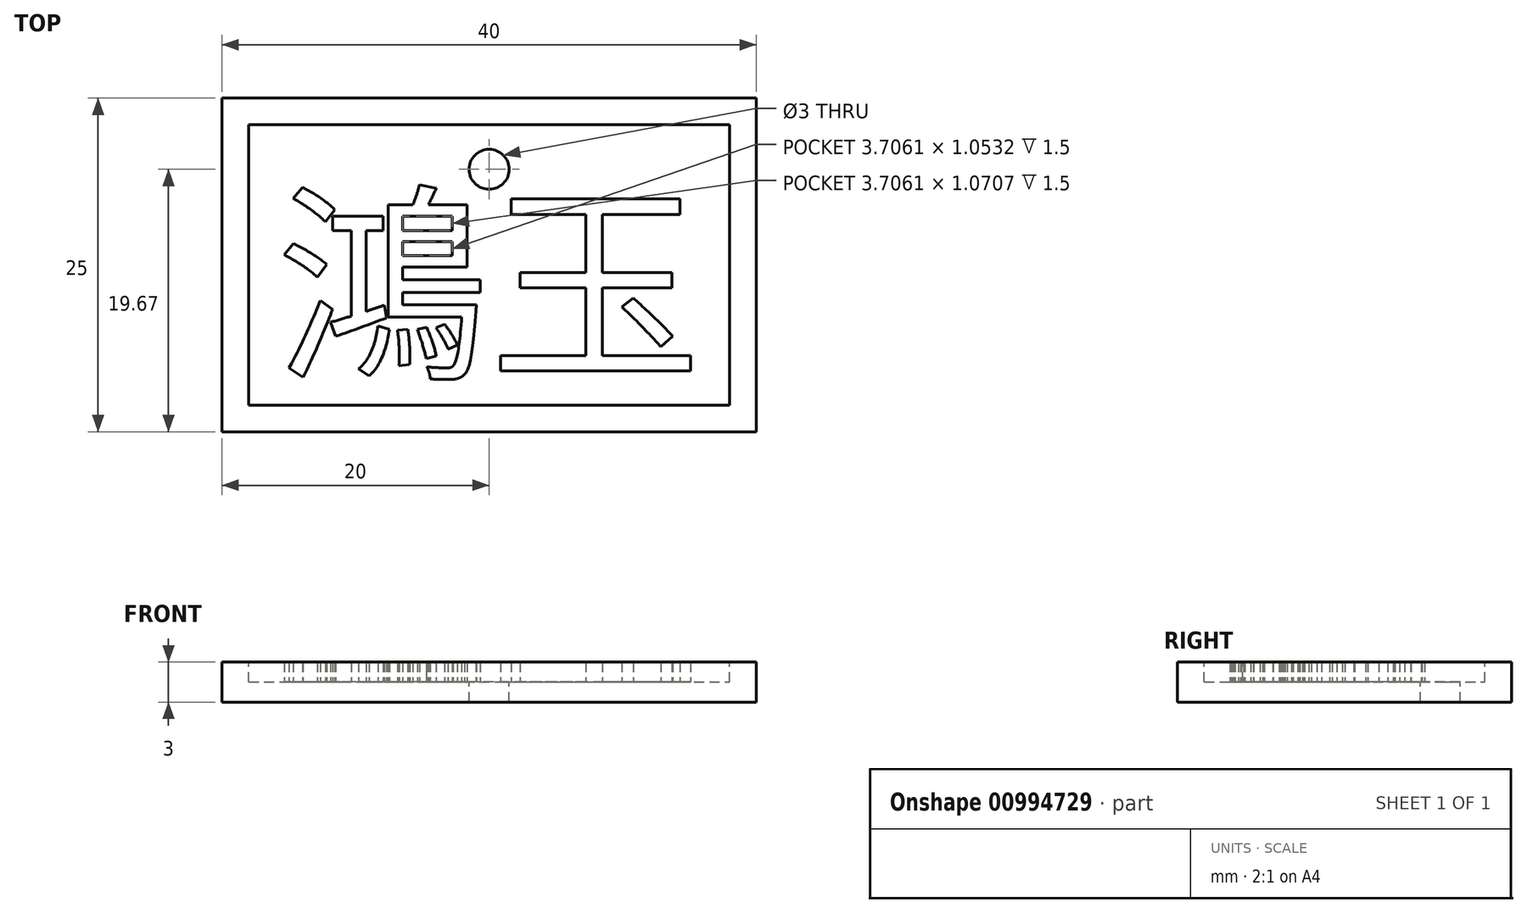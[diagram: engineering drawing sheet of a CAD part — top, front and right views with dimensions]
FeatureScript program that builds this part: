
annotation { "Feature Type Name" : "Feature", "Feature Type Description" : "" }
export const myFeature = defineFeature(function(context is Context, id is Id, definition is map)
    precondition{}
    {
        {
            var Q0;
            Q0=qCreatedBy(makeId("Top.planeOp"),FACE);
            var sketch = newSketch(context, id + "F0", { "sketchPlane" : qUnion([Q0])});
            skLineSegment(sketch, "E0.bottom", {"start": v(20, -12.5) * mm, "end": v(-20, -12.5) * mm});
            skLineSegment(sketch, "E0.top", {"start": v(20, 12.5) * mm, "end": v(-20, 12.5) * mm});
            skLineSegment(sketch, "E0.left", {"start": v(20, -12.5) * mm, "end": v(20, 12.5) * mm});
            skLineSegment(sketch, "E0.right", {"start": v(-20, -12.5) * mm, "end": v(-20, 12.5) * mm});
            skPoint(sketch, "E0.middle", {"position": v(0, 0) * mm});
            skSolve(sketch);
        }
        {
            var Q0;
            Q0 = qSketchRegion(id + "F0", true);
            extrude(context, id + "F1", {"entities" : qUnion([Q0]), "depth" : 3 * mm, "offsetDistance" : 25 * mm});
        }
        {
            var Q0;
            Q0=makeQuery(id+"F1.opExtrude","CAP_FACE",FACE,{"disambiguationData":[OSD([sQuery(id+"F0.wireOp",EDGE,"E0.bottom"),sQuery(id+"F0.wireOp",EDGE,"E0.top"),sQuery(id+"F0.wireOp",EDGE,"E0.left"),sQuery(id+"F0.wireOp",EDGE,"E0.right")])],"isStart":false});
            var sketch = newSketch(context, id + "F2", { "sketchPlane" : qUnion([Q0])});
            skLineSegment(sketch, "E1.0", {"start": v(18, -10.5) * mm, "end": v(18, 10.5) * mm});
            skLineSegment(sketch, "E1.1", {"start": v(-18, -10.5) * mm, "end": v(18, -10.5) * mm});
            skLineSegment(sketch, "E1.2", {"start": v(-18, 10.5) * mm, "end": v(-18, -10.5) * mm});
            skLineSegment(sketch, "E1.3", {"start": v(18, 10.5) * mm, "end": v(-18, 10.5) * mm});
            skSolve(sketch);
        }
        {
            var Q0;
            Q0=makeQuery(id+"F2.imprint","IMPRINT",FACE,{"disambiguationData":[TD([[makeQuery(id+"F2.imprint","IMPRINT",EDGE,{"derivedFrom":sQuery(id+"F2.wireOp",EDGE,"E1.0")}),1.0]])]});
            extrude(context, id + "F3", {"entities" : qUnion([Q0]), "operationType" : NewBodyOperationType.REMOVE, "oppositeDirection" : true, "depth" : 1.5 * mm, "offsetDistance" : 25 * mm});
        }
        {
            var Q0;
            Q0=makeQuery(id+"F3.boolean.opBoolean","COPY",FACE,{"derivedFrom":makeQuery(id+"F3.opExtrude","CAP_FACE",FACE,{"disambiguationData":[OSD([sQuery(id+"F2.wireOp",EDGE,"E1.0"),sQuery(id+"F2.wireOp",EDGE,"E1.1"),sQuery(id+"F2.wireOp",EDGE,"E1.2"),sQuery(id+"F2.wireOp",EDGE,"E1.3")])],"isStart":false})});
            var sketch = newSketch(context, id + "F4", { "sketchPlane" : qUnion([Q0])});
            skCircle(sketch, "E2", {"center": v(0, 7.17) * mm, "radius": 1.5 * mm});
            skSolve(sketch);
        }
        {
            var Q0;
            Q0 = qSketchRegion(id + "F4", true);
            extrude(context, id + "F5", {"entities" : qUnion([Q0]), "operationType" : NewBodyOperationType.REMOVE, "endBound" : BoundingType.THROUGH_ALL, "oppositeDirection" : true, "depth" : 25 * mm, "offsetDistance" : 25 * mm});
        }
        {
            var Q0;
            Q0=makeQuery(id+"F3.boolean.opBoolean","COPY",FACE,{"derivedFrom":makeQuery(id+"F3.opExtrude","CAP_FACE",FACE,{"disambiguationData":[OSD([sQuery(id+"F2.wireOp",EDGE,"E1.0"),sQuery(id+"F2.wireOp",EDGE,"E1.1"),sQuery(id+"F2.wireOp",EDGE,"E1.2"),sQuery(id+"F2.wireOp",EDGE,"E1.3")])],"isStart":false})});
            var sketch = newSketch(context, id + "F6", { "sketchPlane" : qUnion([Q0])});
            skSolve(sketch);
        }
        {
            var Q0;
            Q0=makeQuery(id+"F6.imprint","IMPRINT",FACE,{"disambiguationData":[TD([[makeQuery(id+"F6.imprint","IMPRINT",EDGE,{"derivedFrom":makeQuery(id+"F3.boolean.opBoolean","COPY",EDGE,{"derivedFrom":makeQuery(id+"F3.opExtrude","CAP_EDGE",EDGE,{"disambiguationData":[OSD([sQuery(id+"F2.wireOp",EDGE,"E1.0")])],"isStart":false})})}),1.0]])]});
            var sketch = newSketch(context, id + "F7", { "sketchPlane" : qUnion([Q0])});
            skText(sketch, "E3", { "text": "鴻玉", "fontName": "NotoSansCJKtc-Regular.otf"});
            const initialGuessF7  = {"E3": [-0.016, -0.00736, 1, 0, 0.0115]};
            skSetInitialGuess(sketch, initialGuessF7);
            skSolve(sketch);
        }
        {
            var Q0;
            Q0 = qSketchRegion(id + "F7", true);
            extrude(context, id + "F8", {"entities" : qUnion([Q0]), "operationType" : NewBodyOperationType.ADD, "depth" : 1.5 * mm, "offsetDistance" : 25 * mm});
        }
    });
